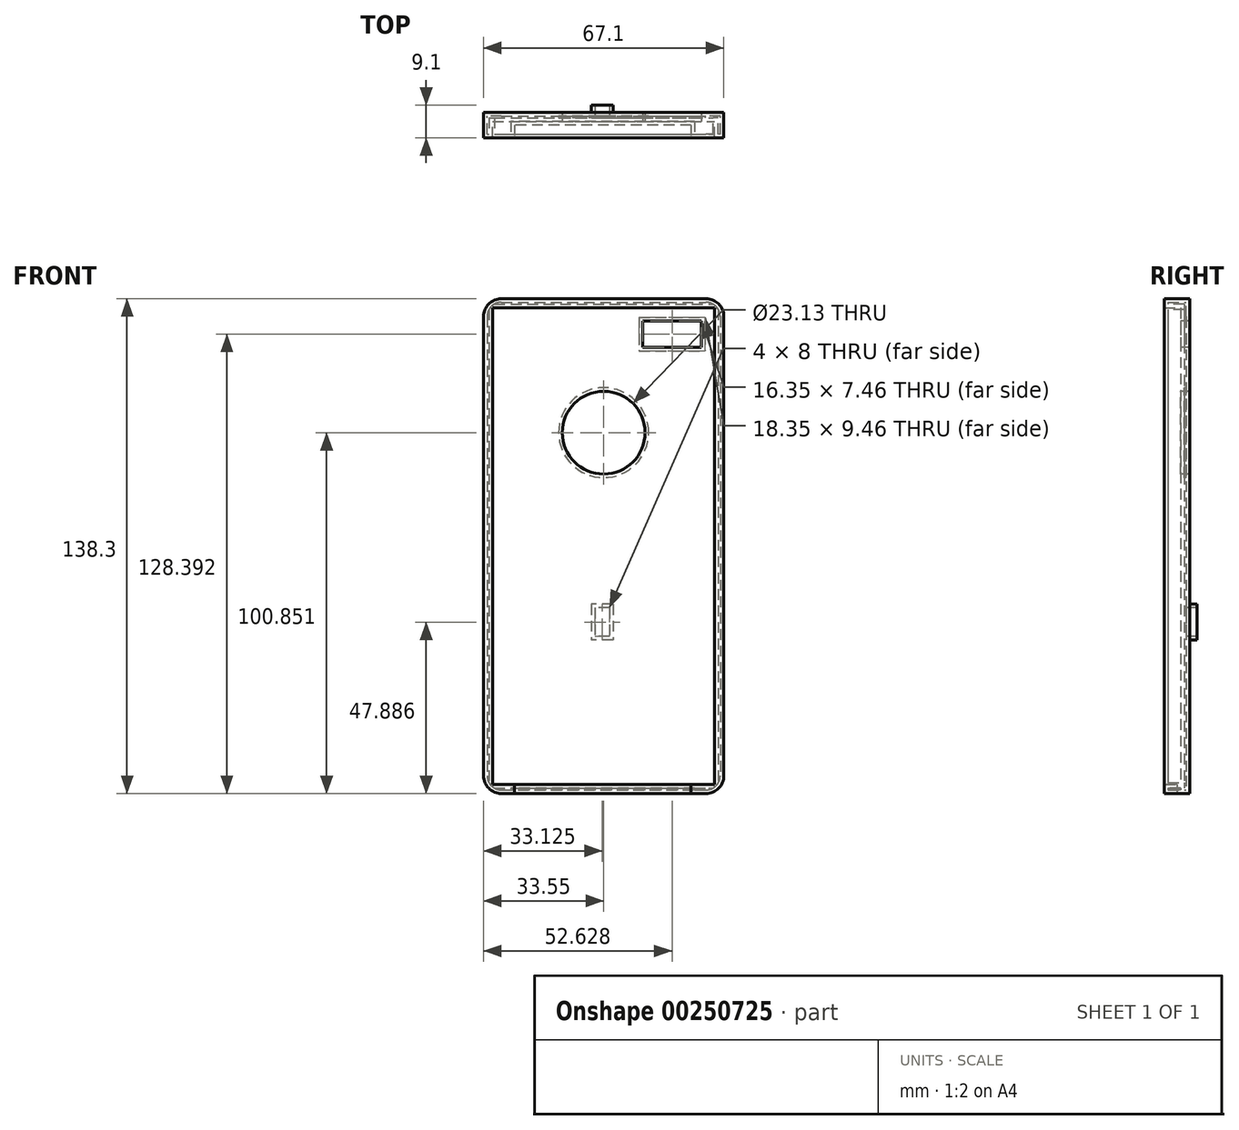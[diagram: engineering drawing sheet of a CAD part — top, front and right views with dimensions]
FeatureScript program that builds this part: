
annotation { "Feature Type Name" : "Feature", "Feature Type Description" : "" }
export const myFeature = defineFeature(function(context is Context, id is Id, definition is map)
    precondition{}
    {
        {
            var Q0;
            Q0=qCreatedBy(makeId("Front.planeOp"),FACE);
            var sketch = newSketch(context, id + "F0", { "sketchPlane" : qUnion([Q0])});
            skLineSegment(sketch, "E0.bottom", {"start": v(-33.55, 69.15) * mm, "end": v(33.55, 69.15) * mm});
            skLineSegment(sketch, "E0.top", {"start": v(-33.55, -69.15) * mm, "end": v(33.55, -69.15) * mm});
            skLineSegment(sketch, "E0.left", {"start": v(-33.55, 69.15) * mm, "end": v(-33.55, -69.15) * mm});
            skLineSegment(sketch, "E0.right", {"start": v(33.55, 69.15) * mm, "end": v(33.55, -69.15) * mm});
            skPoint(sketch, "E0.middle", {"position": v(0, 0) * mm});
            skSolve(sketch);
        }
        {
            var Q0;
            Q0 = qSketchRegion(id + "F0", true);
            extrude(context, id + "F1", {"entities" : qUnion([Q0]), "endBound" : BoundingType.SYMMETRIC, "depth" : 7.1 * mm});
        }
        {
            var Q0;
            Q0=makeQuery(id+"F1.opExtrude","CAP_FACE",FACE,{"disambiguationData":[OSD([sQuery(id+"F0.wireOp",EDGE,"E0.bottom"),sQuery(id+"F0.wireOp",EDGE,"E0.top"),sQuery(id+"F0.wireOp",EDGE,"E0.left"),sQuery(id+"F0.wireOp",EDGE,"E0.right")])],"isStart":false});
            shell(context, id + "F2", {"entities" : qUnion([Q0]), "thickness" : 2.54 * mm});
        }
        {
            var Q0;
            Q0=makeQuery(id+"F1.opExtrude","SWEPT_EDGE",EDGE,{"disambiguationData":[OSD([sQuery(id+"F0.wireOp",EDGE,"E0.bottom"),sQuery(id+"F0.wireOp",EDGE,"E0.left")])]});
            var Q1;
            Q1=makeQuery(id+"F1.opExtrude","SWEPT_EDGE",EDGE,{"disambiguationData":[OSD([sQuery(id+"F0.wireOp",EDGE,"E0.top"),sQuery(id+"F0.wireOp",EDGE,"E0.left")])]});
            var Q2;
            Q2=makeQuery(id+"F1.opExtrude","SWEPT_EDGE",EDGE,{"disambiguationData":[OSD([sQuery(id+"F0.wireOp",EDGE,"E0.bottom"),sQuery(id+"F0.wireOp",EDGE,"E0.right")])]});
            var Q3;
            Q3=makeQuery(id+"F1.opExtrude","SWEPT_EDGE",EDGE,{"disambiguationData":[OSD([sQuery(id+"F0.wireOp",EDGE,"E0.top"),sQuery(id+"F0.wireOp",EDGE,"E0.right")])]});
            fillet(context, id + "F3", {"entities" : qUnion([Q0, Q1, Q2, Q3]), "radius" : 5 * mm, "tangentPropagation" : true, "allowEdgeOverflow" : false});
        }
        {
            var Q0;
            Q0=makeQuery(id+"F2.opShell","OFFSET_FACE",FACE,{"disambiguationData":[OSD([sQuery(id+"F0.wireOp",EDGE,"E0.bottom"),sQuery(id+"F0.wireOp",EDGE,"E0.top"),sQuery(id+"F0.wireOp",EDGE,"E0.left"),sQuery(id+"F0.wireOp",EDGE,"E0.right")])]});
            var sketch = newSketch(context, id + "F4", { "sketchPlane" : qUnion([Q0])});
            skLineSegment(sketch, "E1.bottom", {"start": v(10.9, 62.97) * mm, "end": v(27.25, 62.97) * mm});
            skLineSegment(sketch, "E1.top", {"start": v(10.9, 55.51) * mm, "end": v(27.25, 55.51) * mm});
            skLineSegment(sketch, "E1.left", {"start": v(10.9, 62.97) * mm, "end": v(10.9, 55.51) * mm});
            skLineSegment(sketch, "E1.right", {"start": v(27.25, 62.97) * mm, "end": v(27.25, 55.51) * mm});
            skSolve(sketch);
        }
        {
            var Q0;
            Q0=makeQuery(id+"F4.imprint","IMPRINT",FACE,{"disambiguationData":[TD([[makeQuery(id+"F4.imprint","IMPRINT",EDGE,{"derivedFrom":sQuery(id+"F4.wireOp",EDGE,"E1.bottom")}),-1.0]])]});
            extrude(context, id + "F5", {"entities" : qUnion([Q0]), "operationType" : NewBodyOperationType.REMOVE, "endBound" : BoundingType.SYMMETRIC, "oppositeDirection" : true, "depth" : 25 * mm});
        }
        {
            var Q0;
            Q0=makeQuery(id+"F1.opExtrude","SWEPT_FACE",FACE,{"disambiguationData":[OSD([sQuery(id+"F0.wireOp",EDGE,"E0.top")])]});
            var sketch = newSketch(context, id + "F6", { "sketchPlane" : qUnion([Q0])});
            skPoint(sketch, "E2.oppositeSnap0", {"position": v(28.55, 0) * mm});
            skLineSegment(sketch, "E2.bottom", {"start": v(-24.96, 3.55) * mm, "end": v(24.39, 3.55) * mm});
            skLineSegment(sketch, "E2.top", {"start": v(-24.96, 0) * mm, "end": v(24.39, 0) * mm});
            skLineSegment(sketch, "E2.left", {"start": v(-24.96, 3.55) * mm, "end": v(-24.96, 0) * mm});
            skLineSegment(sketch, "E2.right", {"start": v(24.39, 3.55) * mm, "end": v(24.39, 0) * mm});
            skSolve(sketch);
        }
        {
            var Q0;
            Q0=makeQuery(id+"F6.imprint","IMPRINT",FACE,{"disambiguationData":[TD([[makeQuery(id+"F6.imprint","IMPRINT",EDGE,{"derivedFrom":sQuery(id+"F6.wireOp",EDGE,"E2.bottom")}),-1.0]])]});
            extrude(context, id + "F7", {"entities" : qUnion([Q0]), "operationType" : NewBodyOperationType.REMOVE, "endBound" : BoundingType.SYMMETRIC, "oppositeDirection" : true, "depth" : 25 * mm});
        }
        {
            var Q0;
            Q0=makeQuery(id+"F2.opShell","OFFSET_FACE",FACE,{"disambiguationData":[OSD([sQuery(id+"F0.wireOp",EDGE,"E0.bottom"),sQuery(id+"F0.wireOp",EDGE,"E0.top"),sQuery(id+"F0.wireOp",EDGE,"E0.left"),sQuery(id+"F0.wireOp",EDGE,"E0.right")])]});
            var sketch = newSketch(context, id + "F8", { "sketchPlane" : qUnion([Q0])});
            skCircle(sketch, "E3", {"center": v(0, 31.7) * mm, "radius": 11.56 * mm});
            skSolve(sketch);
        }
        {
            var Q0;
            Q0=makeQuery(id+"F8.imprint","IMPRINT",FACE,{"disambiguationData":[TD([[makeQuery(id+"F8.imprint","IMPRINT",EDGE,{"derivedFrom":sQuery(id+"F8.wireOp",EDGE,"E3")}),1.0]])]});
            extrude(context, id + "F9", {"entities" : qUnion([Q0]), "operationType" : NewBodyOperationType.REMOVE, "endBound" : BoundingType.SYMMETRIC, "oppositeDirection" : true, "depth" : 25 * mm});
        }
        {
            var Q0;
            Q0=makeQuery(id+"F1.opExtrude","CAP_FACE",FACE,{"disambiguationData":[OSD([sQuery(id+"F0.wireOp",EDGE,"E0.bottom"),sQuery(id+"F0.wireOp",EDGE,"E0.top"),sQuery(id+"F0.wireOp",EDGE,"E0.left"),sQuery(id+"F0.wireOp",EDGE,"E0.right")])],"isStart":true});
            var sketch = newSketch(context, id + "F10", { "sketchPlane" : qUnion([Q0])});
            skLineSegment(sketch, "E4.bottom", {"start": v(-2.58, -16.26) * mm, "end": v(3.42, -16.26) * mm});
            skLineSegment(sketch, "E4.top", {"start": v(-2.58, -26.26) * mm, "end": v(3.42, -26.26) * mm});
            skLineSegment(sketch, "E4.left", {"start": v(-2.58, -16.26) * mm, "end": v(-2.58, -26.26) * mm});
            skLineSegment(sketch, "E4.right", {"start": v(3.42, -16.26) * mm, "end": v(3.42, -26.26) * mm});
            skSolve(sketch);
        }
        {
            var Q0;
            Q0=makeQuery(id+"F10.imprint","IMPRINT",FACE,{"disambiguationData":[TD([[makeQuery(id+"F10.imprint","IMPRINT",EDGE,{"derivedFrom":sQuery(id+"F10.wireOp",EDGE,"E4.bottom")}),-1.0]])]});
            extrude(context, id + "F11", {"entities" : qUnion([Q0]), "operationType" : NewBodyOperationType.ADD, "depth" : 2 * mm});
        }
        {
            var Q0;
            Q0=makeQuery(id+"F11.opExtrude","CAP_FACE",FACE,{"disambiguationData":[OSD([sQuery(id+"F10.wireOp",EDGE,"E4.bottom"),sQuery(id+"F10.wireOp",EDGE,"E4.top"),sQuery(id+"F10.wireOp",EDGE,"E4.left"),sQuery(id+"F10.wireOp",EDGE,"E4.right")])],"isStart":false});
            shell(context, id + "F12", {"entities" : qUnion([Q0]), "thickness" : 1 * mm});
        }
    });
